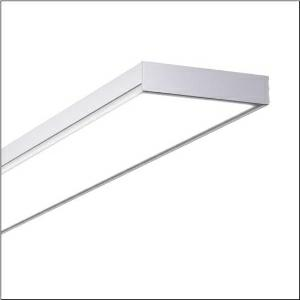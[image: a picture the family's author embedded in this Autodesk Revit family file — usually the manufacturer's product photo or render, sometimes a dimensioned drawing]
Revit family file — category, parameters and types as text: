
# Revit family: apollon_r__31_surface_51mp25wd2441ea_850e
name_source: partatom
category: Lighting Fixtures
units: mm (PartAtom-declared; Revit-internal decimal feet)

## family parameters
Cut with Voids When Loaded = No
Host = Face
Light Source = No
Part Type = Normal
Room Calculation Point = No
Round Connector Dimension = Use Diameter
Shared = No

## types (1)
- Apollon® 31 Surface (1 x LED, 3800 lm, 28 W, 4000K)
    Apparent Load = 28 VA
    CIE Flux Codes = 61 87 97 97 100
    Color Rendering = 80
    Color Temperature = 4000K
    Default Elevation = 1800 mm
    Description = Apollon® 31 Surface, office luminaire, primary optical cover: micro prismatic cover, of PMMA, light emission: direct distribution, primary light characteristic: symmetric, installation type: surface-mounted, LED, rated luminous flux: 3.800lm, luminous efficacy: 134lm/W, light colour: 840, colour temperature: 4000K, control gear: DALI 2, with terminal, 5-pole, mains connection: 220..240V, AC, 50/60Hz, rated input power: 28W, housing, of sheet steel, coil coated, metallic grey (RAL 9006), length: 1.245mm, width: 200mm, height: 44mm, protection rating (complete): IP20, insulation class (complete): insulation class II (safety insulation), certification: CE, impact resistance: IK02, permissible operating ambient temperature: -20..+40°C, standard: EN 60598-2-22, packaging unit: 1 piece
    Height = 44 mm
    Lamp = 1 x LED
    Lamp Light Flux = 3800 lm
    Lamp Power = 28 W
    Lamp count = 1
    Length = 1245 mm
    Luminous efficacy = 136 lm/W
    Manufacturer = Siteco
    ModVariant = No
    Model = 51MP25WD2441EA
    Mounting Place = Ceiling
    Mounting Type = Surface mounted
    Number of Poles = 1
    OnlyDefault = Yes
    Power Factor = 1
    Product Name = Apollon® 31 Surface
    Product group = office luminaire | ceiling mounted
    ProductGroupID = 302
    Protection Class = Protection class II
    Protection Degree = IP 20
    RLX_Detail_Level = 1
    RLX_Emergency_Light_Flux = 0 lm
    RLX_Emergency_Type = 0
    RLX_Emergency_Type_DB = No
    RlxData = <blob elided: 24069 chars, md5=cce2f09b>
    Socket = socket
    Standby Power = 0 W
    System Light Flux = 3800 lm
    System Power = 28 W
    Type Comments = Product without accessories
    Type Image = l_1313654.jpg
    URL = http://relux.com
    VarID = ---
    Voltage = 0 V
    Weight = 0.00 kg
    Width = 200 mm  [stored 0.656168 ft]

note: [stored X ft] marks values corroborated as IEEE doubles in the binary element streams (Revit-internal decimal feet)

## geometry (parser evidence)
native form markers: Blend x4, Sweep x11
no freeform markers — native parametric forms only
